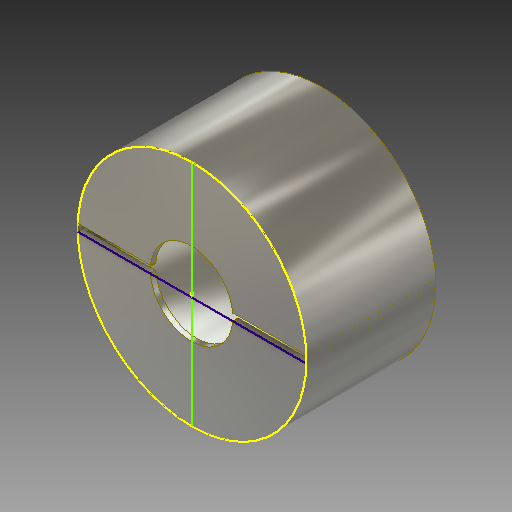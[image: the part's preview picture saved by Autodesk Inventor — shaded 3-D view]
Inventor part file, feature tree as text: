
AUTODESK INVENTOR PART (.ipt)
format: ipt  version: 2018 (Build 220112000, 112)  size: 168,448 bytes
history: native  units: in
note: dims shown in document units (in); Inventor stores cm internally (conversion verified against a paired STEP export)
features: extrude x4, sketch x2, shell x1
ambient origin geometry x8: Origin, YZ Plane, XZ Plane, XY Plane, X Axis, Y Axis, Z Axis, Center Point
bodies: Solid1 (feature_tree)
feature tree (7):
  sketch  "Sketch1"  dims[d0=0.65in d1=0.369in d2=0.0in d3=0.015in]
  extrude  "Extrusion1"  Depth=0.369in TaperAngle=0.0deg
  shell  "Shell1"  Thickness=0.015in
  extrude  "Extrusion3"  Depth=0.02in
  extrude  "Extrusion4"  Depth=0.02in TaperAngle=0.0deg
  extrude  "Extrusion5"  Depth=0.02in TaperAngle=0.0deg
  sketch  "Sketch2"  dims[d13=0.235in d14=0.02in d17=0.69in d18=0.0in d19=0.69in d20=0.0in d21=0.69in d22=0.0in]
